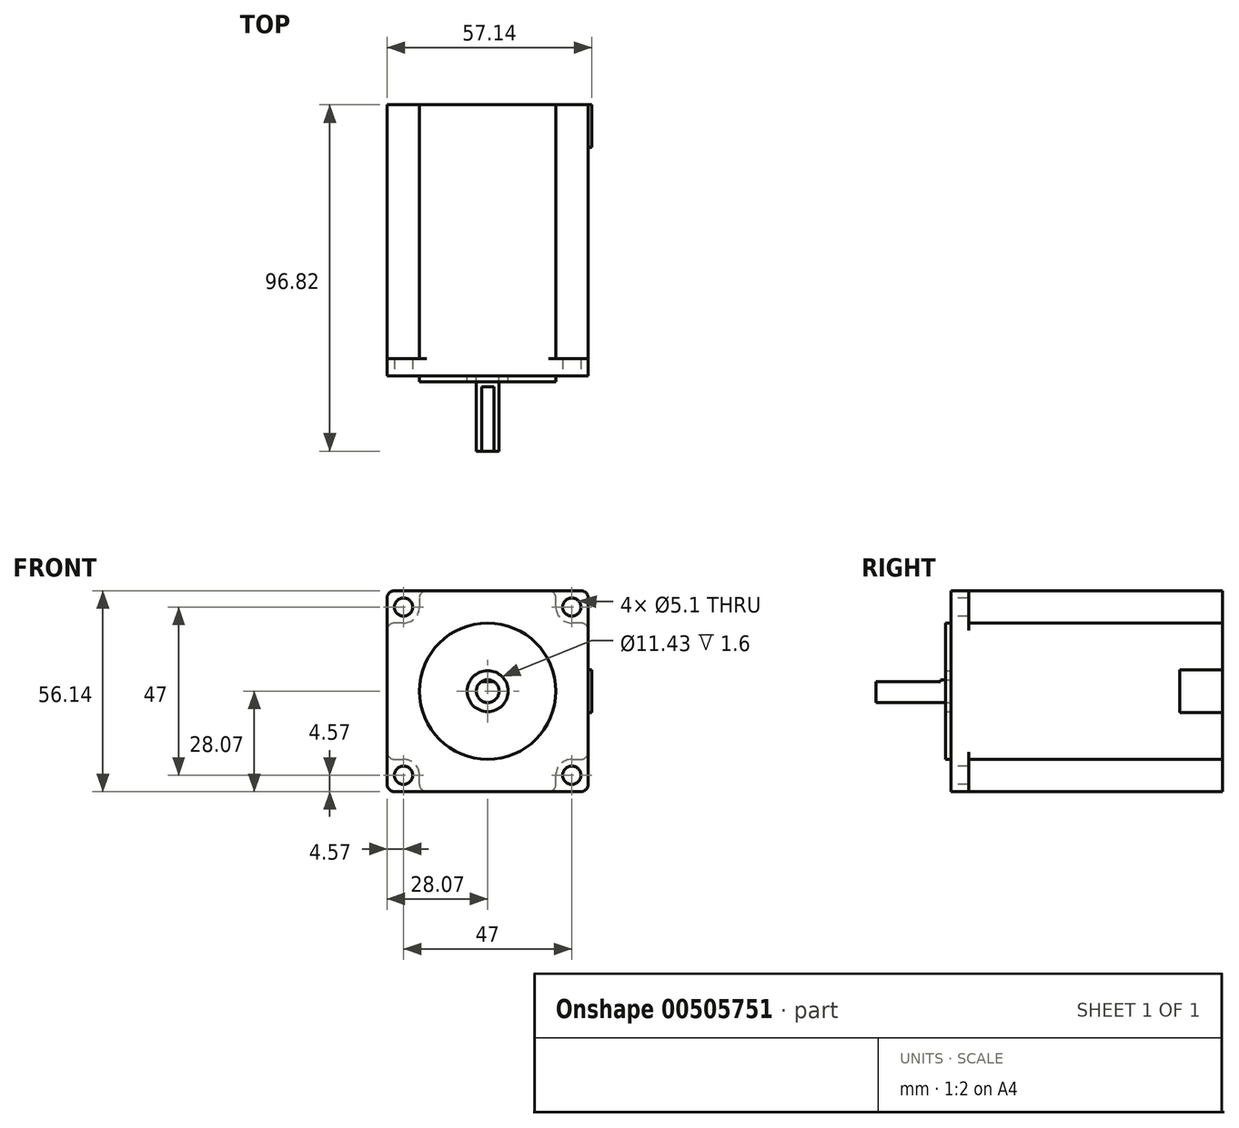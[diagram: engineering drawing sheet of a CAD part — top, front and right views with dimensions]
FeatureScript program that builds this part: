
annotation { "Feature Type Name" : "Feature", "Feature Type Description" : "" }
export const myFeature = defineFeature(function(context is Context, id is Id, definition is map)
    precondition{}
    {
        {
            var Q0;
            Q0=qCreatedBy(makeId("Front.planeOp"),FACE);
            var sketch = newSketch(context, id + "F0", { "sketchPlane" : qUnion([Q0])});
            skCircle(sketch, "E0", {"center": v(0, 0) * mm, "radius": 19.05 * mm});
            skLineSegment(sketch, "E1.bottom", {"start": v(-28.07, 28.07) * mm, "end": v(28.07, 28.07) * mm});
            skLineSegment(sketch, "E1.top", {"start": v(-28.07, -28.07) * mm, "end": v(28.07, -28.07) * mm});
            skLineSegment(sketch, "E1.left", {"start": v(-28.07, 28.07) * mm, "end": v(-28.07, -28.07) * mm});
            skLineSegment(sketch, "E1.right", {"start": v(28.07, 28.07) * mm, "end": v(28.07, -28.07) * mm});
            skPoint(sketch, "E2", {"position": v(-28.07, 0) * mm});
            skPoint(sketch, "E3", {"position": v(0, 28.07) * mm});
            skLineSegment(sketch, "E4.bottom", {"start": v(-23.5, 23.5) * mm, "end": v(23.5, 23.5) * mm, "construction": true});
            skLineSegment(sketch, "E4.top", {"start": v(-23.5, -23.5) * mm, "end": v(23.5, -23.5) * mm, "construction": true});
            skLineSegment(sketch, "E4.left", {"start": v(-23.5, 23.5) * mm, "end": v(-23.5, -23.5) * mm, "construction": true});
            skLineSegment(sketch, "E4.right", {"start": v(23.5, 23.5) * mm, "end": v(23.5, -23.5) * mm, "construction": true});
            skPoint(sketch, "E5", {"position": v(-23.5, 0) * mm});
            skPoint(sketch, "E6", {"position": v(0, 23.5) * mm});
            skCircle(sketch, "E7", {"center": v(-23.5, 23.5) * mm, "radius": 2.55 * mm});
            skCircle(sketch, "E8", {"center": v(23.5, 23.5) * mm, "radius": 2.55 * mm});
            skCircle(sketch, "E9", {"center": v(-23.5, -23.5) * mm, "radius": 2.55 * mm});
            skCircle(sketch, "E10", {"center": v(23.5, -23.5) * mm, "radius": 2.55 * mm});
            skCircle(sketch, "E11", {"center": v(0, 0) * mm, "radius": 5.72 * mm});
            skCircle(sketch, "E12", {"center": v(0, 0) * mm, "radius": 3.18 * mm});
            skLineSegment(sketch, "E13", {"start": v(-1.71, 2.67) * mm, "end": v(1.71, 2.67) * mm});
            skPoint(sketch, "E14", {"position": v(0, -3.18) * mm});
            skSolve(sketch);
        }
        {
            var Q0;
            {var subQ0=sQuery(id+"F0.wireOp",EDGE,"E13");Q0=makeQuery(id+"F0.imprint","IMPRINT",FACE,{"disambiguationData":[TD([[makeQuery(id+"F0.imprint","IMPRINT",EDGE,{"derivedFrom":subQ0}),-1.0]])]});}
            extrude(context, id + "F1", {"entities" : qUnion([Q0]), "depth" : 21 * mm});
        }
        {
            var Q0;
            {var subQ0=sQuery(id+"F0.wireOp",EDGE,"E13");Q0=makeQuery(id+"F0.imprint","IMPRINT",FACE,{"disambiguationData":[TD([[makeQuery(id+"F0.imprint","IMPRINT",EDGE,{"derivedFrom":subQ0}),1.0]])]});}
            var Q1;
            {var subQ0=sQuery(id+"F0.wireOp",EDGE,"E13");Q1=makeQuery(id+"F0.imprint","IMPRINT",FACE,{"disambiguationData":[TD([[makeQuery(id+"F0.imprint","IMPRINT",EDGE,{"derivedFrom":subQ0}),-1.0]])]});}
            extrude(context, id + "F2", {"entities" : qUnion([Q0, Q1]), "operationType" : NewBodyOperationType.ADD, "endBound" : BoundingType.SYMMETRIC, "depth" : 6 * mm});
        }
        {
            var Q0;
            Q0=makeQuery(id+"F0.imprint","IMPRINT",FACE,{"disambiguationData":[TD([[makeQuery(id+"F0.imprint","IMPRINT",EDGE,{"derivedFrom":sQuery(id+"F0.wireOp",EDGE,"E0")}),1.0]])]});
            extrude(context, id + "F3", {"entities" : qUnion([Q0]), "depth" : 1.6 * mm, "hasSecondDirection" : true, "secondDirectionOppositeDirection" : true, "secondDirectionDepth" : 10 * mm});
        }
        {
            var Q0;
            Q0=makeQuery(id+"F0.imprint","IMPRINT",FACE,{"disambiguationData":[TD([[makeQuery(id+"F0.imprint","IMPRINT",EDGE,{"derivedFrom":sQuery(id+"F0.wireOp",EDGE,"E0")}),-1.0]])]});
            extrude(context, id + "F4", {"entities" : qUnion([Q0]), "operationType" : NewBodyOperationType.ADD, "oppositeDirection" : true, "depth" : 4.9 * mm});
        }
        {
            var Q0;
            Q0=qCreatedBy(makeId("Front.planeOp"),FACE);
            var sketch = newSketch(context, id + "F5", { "sketchPlane" : qUnion([Q0])});
            skLineSegment(sketch, "E15.0", {"start": v(-28.07, 28.07) * mm, "end": v(-28.07, -28.07) * mm, "construction": true});
            skCircle(sketch, "E15.1", {"center": v(-23.5, 23.5) * mm, "radius": 2.55 * mm, "construction": true});
            skLineSegment(sketch, "E15.2", {"start": v(-28.07, 28.07) * mm, "end": v(28.07, 28.07) * mm, "construction": true});
            skCircle(sketch, "E15.3", {"center": v(23.5, 23.5) * mm, "radius": 2.55 * mm, "construction": true});
            skLineSegment(sketch, "E15.4", {"start": v(28.07, 28.07) * mm, "end": v(28.07, -28.07) * mm, "construction": true});
            skCircle(sketch, "E15.5", {"center": v(23.5, -23.5) * mm, "radius": 2.55 * mm, "construction": true});
            skLineSegment(sketch, "E15.6", {"start": v(-28.07, -28.07) * mm, "end": v(28.07, -28.07) * mm, "construction": true});
            skCircle(sketch, "E15.7", {"center": v(-23.5, -23.5) * mm, "radius": 2.55 * mm, "construction": true});
            skLineSegment(sketch, "E16.bottom", {"start": v(-19.05, 19.05) * mm, "end": v(19.05, 19.05) * mm, "construction": true});
            skLineSegment(sketch, "E16.top", {"start": v(-19.05, -19.05) * mm, "end": v(19.05, -19.05) * mm, "construction": true});
            skLineSegment(sketch, "E16.left", {"start": v(-19.05, 19.05) * mm, "end": v(-19.05, -19.05) * mm, "construction": true});
            skLineSegment(sketch, "E16.right", {"start": v(19.05, 19.05) * mm, "end": v(19.05, -19.05) * mm, "construction": true});
            skPoint(sketch, "E17", {"position": v(0, 28.07) * mm});
            skPoint(sketch, "E18", {"position": v(-28.07, 0) * mm});
            skPoint(sketch, "E19", {"position": v(-19.05, 0) * mm});
            skPoint(sketch, "E20", {"position": v(0, 19.05) * mm});
            skArc(sketch, "E21", {"start": v(-23.5, 19.05) * mm, "mid": v(-20.35, 20.35) * mm, "end": v(-19.05, 23.5) * mm});
            skArc(sketch, "E22", {"start": v(19.05, 23.5) * mm, "mid": v(20.35, 20.35) * mm, "end": v(23.5, 19.05) * mm});
            skArc(sketch, "E23", {"start": v(23.5, -19.05) * mm, "mid": v(20.35, -20.35) * mm, "end": v(19.05, -23.5) * mm});
            skArc(sketch, "E24", {"start": v(-19.05, -23.5) * mm, "mid": v(-20.35, -20.35) * mm, "end": v(-23.5, -19.05) * mm});
            skLineSegment(sketch, "E25", {"start": v(-28.07, -19.05) * mm, "end": v(-23.5, -19.05) * mm});
            skLineSegment(sketch, "E26", {"start": v(-19.05, -28.07) * mm, "end": v(-19.05, -23.5) * mm});
            skLineSegment(sketch, "E27", {"start": v(19.05, -28.07) * mm, "end": v(19.05, -23.5) * mm});
            skLineSegment(sketch, "E28", {"start": v(23.5, -19.05) * mm, "end": v(28.07, -19.05) * mm});
            skLineSegment(sketch, "E29", {"start": v(28.07, 19.05) * mm, "end": v(23.5, 19.05) * mm});
            skLineSegment(sketch, "E30", {"start": v(19.05, 23.5) * mm, "end": v(19.05, 28.07) * mm});
            skLineSegment(sketch, "E31", {"start": v(-19.05, 28.07) * mm, "end": v(-19.05, 23.5) * mm});
            skLineSegment(sketch, "E32", {"start": v(-23.5, 19.05) * mm, "end": v(-28.07, 19.05) * mm});
            skLineSegment(sketch, "E33", {"start": v(-28.07, 19.05) * mm, "end": v(-28.07, -19.05) * mm});
            skLineSegment(sketch, "E34", {"start": v(-19.05, -28.07) * mm, "end": v(19.05, -28.07) * mm});
            skLineSegment(sketch, "E35", {"start": v(28.07, -19.05) * mm, "end": v(28.07, 19.05) * mm});
            skLineSegment(sketch, "E36", {"start": v(19.05, 28.07) * mm, "end": v(-19.05, 28.07) * mm});
            skSolve(sketch);
        }
        {
            var Q0;
            Q0=makeQuery(id+"F5.imprint","IMPRINT",FACE,{"disambiguationData":[TD([[makeQuery(id+"F5.imprint","IMPRINT",EDGE,{"derivedFrom":sQuery(id+"F5.wireOp",EDGE,"E21")}),-1.0]])]});
            extrude(context, id + "F6", {"entities" : qUnion([Q0]), "operationType" : NewBodyOperationType.ADD, "oppositeDirection" : true, "depth" : 75.82 * mm});
        }
        {
            var Q0;
            Q0=makeQuery(id+"F6.opExtrude","SWEPT_EDGE",EDGE,{"disambiguationData":[OSD([sQuery(id+"F5.wireOp",EDGE,"E30"),sQuery(id+"F5.wireOp",EDGE,"E36")])]});
            var Q1;
            Q1=makeQuery(id+"F6.opExtrude","SWEPT_EDGE",EDGE,{"disambiguationData":[OSD([sQuery(id+"F5.wireOp",EDGE,"E29"),sQuery(id+"F5.wireOp",EDGE,"E35")])]});
            var Q2;
            Q2=makeQuery(id+"F4.opExtrude","SWEPT_EDGE",EDGE,{"disambiguationData":[OSD([sQuery(id+"F0.wireOp",EDGE,"E1.bottom"),sQuery(id+"F0.wireOp",EDGE,"E1.right")])]});
            var Q3;
            Q3=makeQuery(id+"F4.opExtrude","SWEPT_EDGE",EDGE,{"disambiguationData":[OSD([sQuery(id+"F0.wireOp",EDGE,"E1.top"),sQuery(id+"F0.wireOp",EDGE,"E1.right")])]});
            var Q4;
            Q4=makeQuery(id+"F6.opExtrude","SWEPT_EDGE",EDGE,{"disambiguationData":[OSD([sQuery(id+"F5.wireOp",EDGE,"E28"),sQuery(id+"F5.wireOp",EDGE,"E35")])]});
            var Q5;
            Q5=makeQuery(id+"F6.opExtrude","SWEPT_EDGE",EDGE,{"disambiguationData":[OSD([sQuery(id+"F5.wireOp",EDGE,"E27"),sQuery(id+"F5.wireOp",EDGE,"E34")])]});
            var Q6;
            Q6=makeQuery(id+"F6.opExtrude","SWEPT_EDGE",EDGE,{"disambiguationData":[OSD([sQuery(id+"F5.wireOp",EDGE,"E26"),sQuery(id+"F5.wireOp",EDGE,"E34")])]});
            var Q7;
            Q7=makeQuery(id+"F6.opExtrude","SWEPT_EDGE",EDGE,{"disambiguationData":[OSD([sQuery(id+"F5.wireOp",EDGE,"E25"),sQuery(id+"F5.wireOp",EDGE,"E33")])]});
            var Q8;
            Q8=makeQuery(id+"F4.opExtrude","SWEPT_EDGE",EDGE,{"disambiguationData":[OSD([sQuery(id+"F0.wireOp",EDGE,"E1.top"),sQuery(id+"F0.wireOp",EDGE,"E1.left")])]});
            var Q9;
            Q9=makeQuery(id+"F4.opExtrude","SWEPT_EDGE",EDGE,{"disambiguationData":[OSD([sQuery(id+"F0.wireOp",EDGE,"E1.bottom"),sQuery(id+"F0.wireOp",EDGE,"E1.left")])]});
            var Q10;
            Q10=makeQuery(id+"F6.opExtrude","SWEPT_EDGE",EDGE,{"disambiguationData":[OSD([sQuery(id+"F5.wireOp",EDGE,"E32"),sQuery(id+"F5.wireOp",EDGE,"E33")])]});
            var Q11;
            Q11=makeQuery(id+"F6.opExtrude","SWEPT_EDGE",EDGE,{"disambiguationData":[OSD([sQuery(id+"F5.wireOp",EDGE,"E31"),sQuery(id+"F5.wireOp",EDGE,"E36")])]});
            fillet(context, id + "F7", {"entities" : qUnion([Q0, Q1, Q2, Q3, Q4, Q5, Q6, Q7, Q8, Q9, Q10, Q11]), "radius" : 2 * mm, "tangentPropagation" : true, "allowEdgeOverflow" : false});
        }
        {
            var Q0;
            Q0=makeQuery(id+"F6.boolean.opBoolean","MERGE",FACE,{"derivedFrom":[makeQuery(id+"F4.opExtrude","SWEPT_FACE",FACE,{"disambiguationData":[OSD([sQuery(id+"F0.wireOp",EDGE,"E1.right")])]}),makeQuery(id+"F6.opExtrude","SWEPT_FACE",FACE,{"disambiguationData":[OSD([sQuery(id+"F5.wireOp",EDGE,"E35")])]})]});
            var sketch = newSketch(context, id + "F8", { "sketchPlane" : qUnion([Q0])});
            skLineSegment(sketch, "E37.bottom", {"start": v(63.88, 5.97) * mm, "end": v(75.82, 5.97) * mm});
            skLineSegment(sketch, "E37.top", {"start": v(63.88, -5.97) * mm, "end": v(75.82, -5.97) * mm});
            skLineSegment(sketch, "E37.left", {"start": v(63.88, 5.97) * mm, "end": v(63.88, -5.97) * mm});
            skLineSegment(sketch, "E37.right", {"start": v(75.82, 5.97) * mm, "end": v(75.82, -5.97) * mm});
            skPoint(sketch, "E38", {"position": v(75.82, 0) * mm});
            skLineSegment(sketch, "E39.0", {"start": v(75.82, -17.05) * mm, "end": v(75.82, 17.05) * mm, "construction": true});
            skSolve(sketch);
        }
        {
            var Q0;
            Q0=makeQuery(id+"F8.imprint","IMPRINT",FACE,{"disambiguationData":[TD([[makeQuery(id+"F8.imprint","IMPRINT",EDGE,{"derivedFrom":sQuery(id+"F8.wireOp",EDGE,"E37.bottom")}),-1.0]])]});
            extrude(context, id + "F9", {"entities" : qUnion([Q0]), "operationType" : NewBodyOperationType.ADD, "depth" : 1 * mm});
        }
    });
